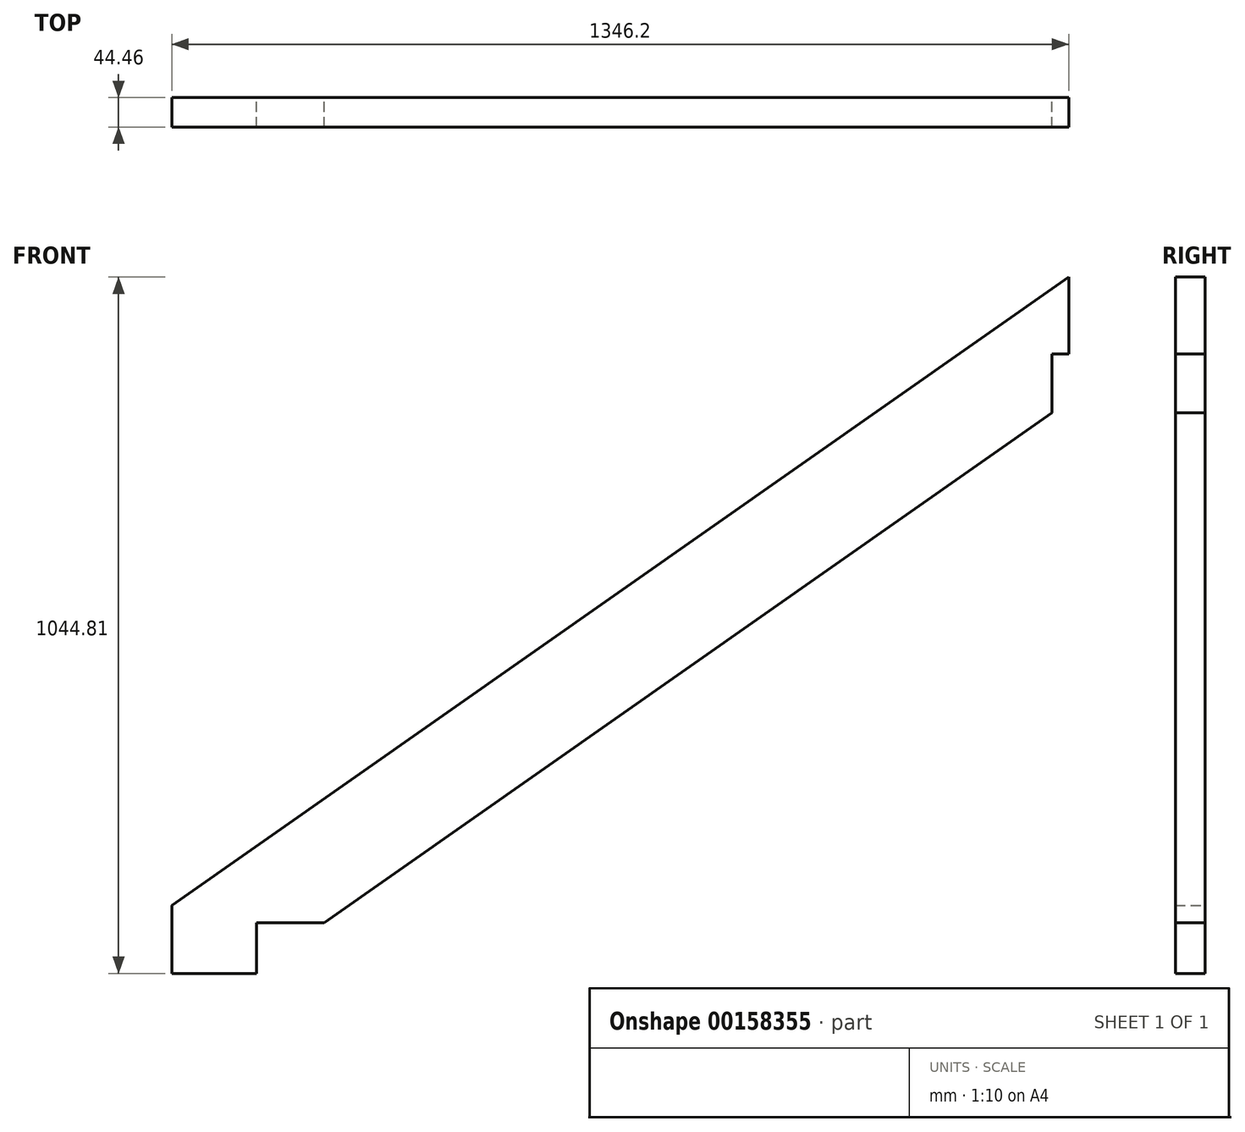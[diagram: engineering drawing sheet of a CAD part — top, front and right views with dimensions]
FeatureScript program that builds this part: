
annotation { "Feature Type Name" : "Feature", "Feature Type Description" : "" }
export const myFeature = defineFeature(function(context is Context, id is Id, definition is map)
    precondition{}
    {
        {
            var Q0;
            Q0=qCreatedBy(makeId("Front.planeOp"),FACE);
            var sketch = newSketch(context, id + "F0", { "sketchPlane" : qUnion([Q0])});
            skLineSegment(sketch, "E0", {"start": v(-1592.45, -622.5) * mm, "end": v(-246.25, 320.13) * mm});
            skLineSegment(sketch, "E1", {"start": v(-1592.45, -622.5) * mm, "end": v(-1592.45, -724.68) * mm});
            skLineSegment(sketch, "E2", {"start": v(-1592.45, -724.68) * mm, "end": v(-1465.45, -724.68) * mm});
            skLineSegment(sketch, "E3", {"start": v(-1465.45, -724.68) * mm, "end": v(-1465.45, -648.48) * mm});
            skLineSegment(sketch, "E4", {"start": v(-1465.45, -648.48) * mm, "end": v(-1363.85, -648.48) * mm});
            skLineSegment(sketch, "E5", {"start": v(-246.25, 320.13) * mm, "end": v(-246.25, 204.7) * mm});
            skLineSegment(sketch, "E6", {"start": v(-246.25, 204.7) * mm, "end": v(-271.65, 204.7) * mm});
            skLineSegment(sketch, "E7", {"start": v(-271.65, 204.7) * mm, "end": v(-271.65, 116.3) * mm});
            skLineSegment(sketch, "E8", {"start": v(-1363.85, -648.48) * mm, "end": v(-271.65, 116.3) * mm});
            skSolve(sketch);
        }
        {
            var Q0;
            Q0=makeQuery(id+"F0.imprint","IMPRINT",FACE,{"disambiguationData":[TD([[makeQuery(id+"F0.imprint","IMPRINT",EDGE,{"derivedFrom":sQuery(id+"F0.wireOp",EDGE,"E0")}),-1.0]])]});
            extrude(context, id + "F1", {"entities" : qUnion([Q0]), "endBound" : BoundingType.SYMMETRIC, "depth" : 44.45 * mm});
        }
    });
